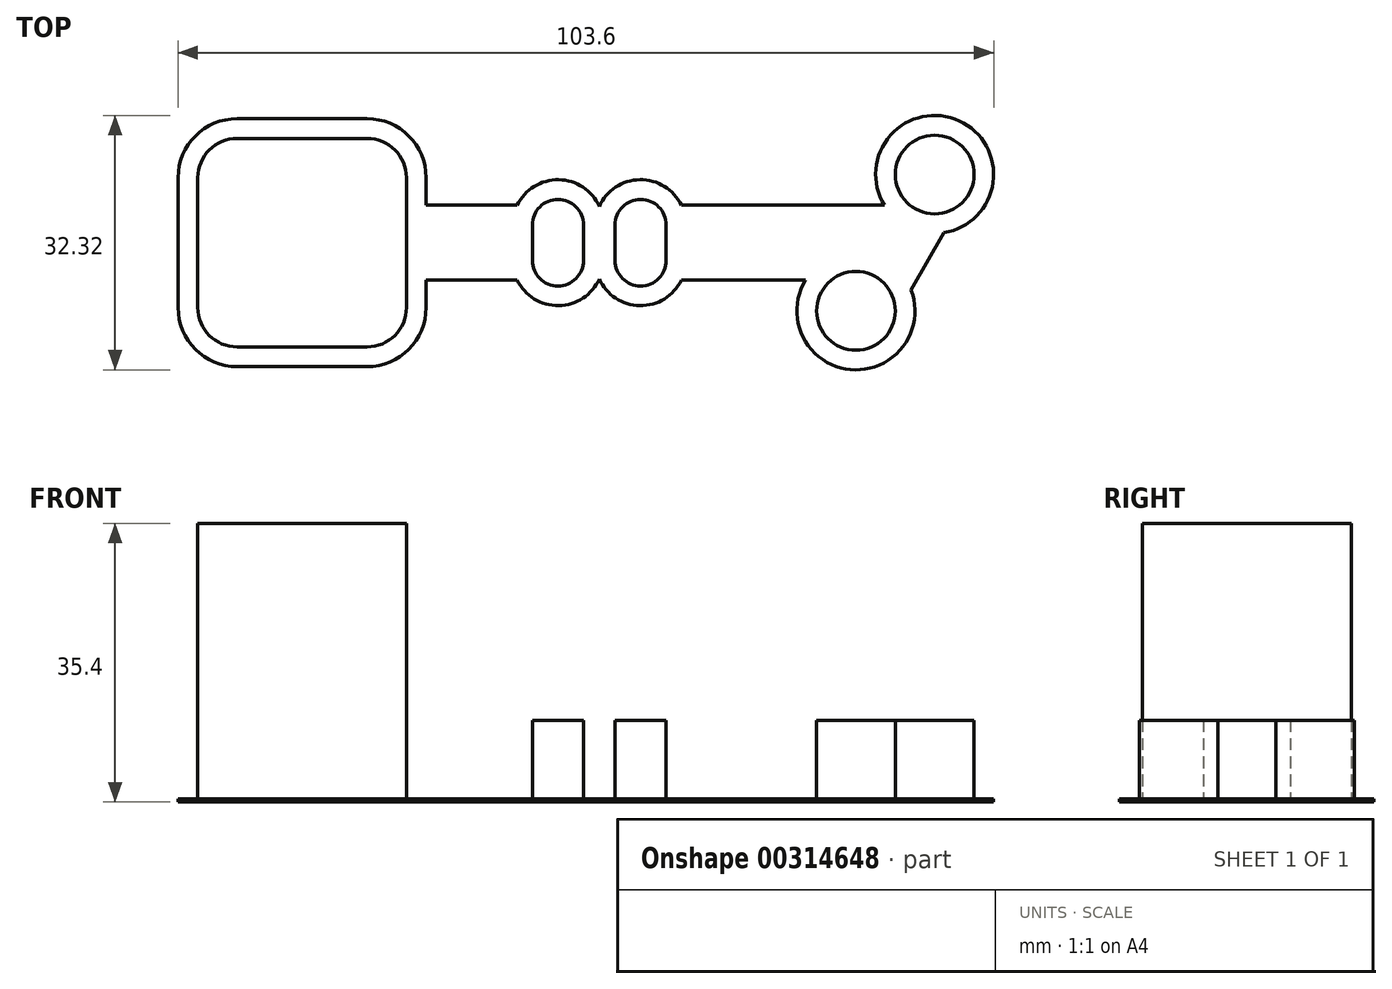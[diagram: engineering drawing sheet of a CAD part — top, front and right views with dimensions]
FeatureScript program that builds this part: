
annotation { "Feature Type Name" : "Feature", "Feature Type Description" : "" }
export const myFeature = defineFeature(function(context is Context, id is Id, definition is map)
    precondition{}
    {
        {
            var Q0;
            Q0=qCreatedBy(makeId("Top.planeOp"),FACE);
            var sketch = newSketch(context, id + "F0", { "sketchPlane" : qUnion([Q0])});
            skLineSegment(sketch, "E0.bottom", {"start": v(-8.25, 13.25) * mm, "end": v(8.25, 13.25) * mm});
            skLineSegment(sketch, "E0.top", {"start": v(-8.25, -13.25) * mm, "end": v(8.25, -13.25) * mm});
            skLineSegment(sketch, "E0.left", {"start": v(-13.25, 8.25) * mm, "end": v(-13.25, -8.25) * mm});
            skLineSegment(sketch, "E0.right", {"start": v(13.25, 8.25) * mm, "end": v(13.25, 2.25) * mm});
            skPoint(sketch, "E0.middle", {"position": v(0, 0) * mm});
            skPoint(sketch, "E1.visualSharp", {"position": v(-13.25, 13.25) * mm});
            skArc(sketch, "E1.filletArc", {"start": v(-8.25, 13.25) * mm, "mid": v(-11.79, 11.79) * mm, "end": v(-13.25, 8.25) * mm});
            skPoint(sketch, "E2.visualSharp", {"position": v(13.25, 13.25) * mm});
            skArc(sketch, "E2.filletArc", {"start": v(13.25, 8.25) * mm, "mid": v(11.79, 11.79) * mm, "end": v(8.25, 13.25) * mm});
            skPoint(sketch, "E3.visualSharp", {"position": v(13.25, -13.25) * mm});
            skArc(sketch, "E3.filletArc", {"start": v(8.25, -13.25) * mm, "mid": v(11.79, -11.79) * mm, "end": v(13.25, -8.25) * mm});
            skPoint(sketch, "E4.visualSharp", {"position": v(-13.25, -13.25) * mm});
            skArc(sketch, "E4.filletArc", {"start": v(-13.25, -8.25) * mm, "mid": v(-11.79, -11.79) * mm, "end": v(-8.25, -13.25) * mm});
            skCircle(sketch, "E5", {"center": v(0, 0) * mm, "radius": 4.5 * mm});
            skLineSegment(sketch, "E6", {"start": v(-4.5, 13.25) * mm, "end": v(-4.5, -13.25) * mm});
            skLineSegment(sketch, "E7", {"start": v(4.5, 13.25) * mm, "end": v(4.5, -13.25) * mm});
            skLineSegment(sketch, "E8", {"start": v(-13.25, 4.5) * mm, "end": v(13.25, 4.5) * mm});
            skLineSegment(sketch, "E9", {"start": v(-13.25, -4.5) * mm, "end": v(13.25, -4.5) * mm});
            skLineSegment(sketch, "E10", {"start": v(-40.84, 0) * mm, "end": v(98.04, 0) * mm, "construction": true});
            skPoint(sketch, "E10.startSnap0", {"position": v(-13.25, 0) * mm});
            skPoint(sketch, "E10.endSnap0", {"position": v(-13.25, 0) * mm});
            skLineSegment(sketch, "E11", {"start": v(13.25, 2.25) * mm, "end": v(29.25, 2.25) * mm});
            skLineSegment(sketch, "E12.bottom", {"start": v(29.25, 2.25) * mm, "end": v(35.75, 2.25) * mm});
            skLineSegment(sketch, "E12.top", {"start": v(29.25, -2.25) * mm, "end": v(35.75, -2.25) * mm});
            skLineSegment(sketch, "E12.left", {"start": v(29.25, 2.25) * mm, "end": v(29.25, -2.25) * mm});
            skLineSegment(sketch, "E12.right", {"start": v(35.75, 2.25) * mm, "end": v(35.75, -2.25) * mm});
            skLineSegment(sketch, "E13", {"start": v(37.75, 18.58) * mm, "end": v(37.75, -20.06) * mm, "construction": true});
            skLineSegment(sketch, "E14.MirrorCS", {"start": v(13.25, -2.25) * mm, "end": v(29.25, -2.25) * mm});
            skLineSegment(sketch, "E15.MirrorCS", {"start": v(46.25, 2.25) * mm, "end": v(39.75, 2.25) * mm});
            skLineSegment(sketch, "E16.MirrorCS", {"start": v(39.75, 2.25) * mm, "end": v(39.75, -2.25) * mm});
            skLineSegment(sketch, "E17.MirrorCS", {"start": v(46.25, -2.25) * mm, "end": v(39.75, -2.25) * mm});
            skLineSegment(sketch, "E18.MirrorCS", {"start": v(46.25, 2.25) * mm, "end": v(46.25, -2.25) * mm});
            skArc(sketch, "E19", {"start": v(29.25, 2.25) * mm, "mid": v(32.5, 5.5) * mm, "end": v(35.75, 2.25) * mm});
            skArc(sketch, "E20.MirrorCS", {"start": v(29.25, -2.25) * mm, "mid": v(32.5, -5.5) * mm, "end": v(35.75, -2.25) * mm});
            skArc(sketch, "E21.MirrorCS", {"start": v(46.25, 2.25) * mm, "mid": v(43, 5.5) * mm, "end": v(39.75, 2.25) * mm});
            skArc(sketch, "E22.MirrorCS", {"start": v(46.25, -2.25) * mm, "mid": v(43, -5.5) * mm, "end": v(39.75, -2.25) * mm});
            skLineSegment(sketch, "E23", {"start": v(35.75, 2.25) * mm, "end": v(39.75, 2.25) * mm});
            skLineSegment(sketch, "E24", {"start": v(39.75, -2.25) * mm, "end": v(35.75, -2.25) * mm});
            skLineSegment(sketch, "E25", {"start": v(46.25, 2.25) * mm, "end": v(74.05, 2.25) * mm});
            skLineSegment(sketch, "E26", {"start": v(80.35, 8.66) * mm, "end": v(70.35, -8.66) * mm, "construction": true});
            skPoint(sketch, "E27", {"position": v(75.35, 0) * mm});
            skLineSegment(sketch, "E28", {"start": v(76.17, 5.92) * mm, "end": v(74.05, 2.25) * mm});
            skLineSegment(sketch, "E29.MirrorCS", {"start": v(80.06, 3.67) * mm, "end": v(74.53, -5.92) * mm});
            skLineSegment(sketch, "E30.MirrorCS", {"start": v(46.25, -2.25) * mm, "end": v(71.45, -2.25) * mm});
            skPoint(sketch, "E31.orphan", {"position": v(72.75, -2.25) * mm});
            skPoint(sketch, "E32", {"position": v(72.75, 0) * mm});
            skLineSegment(sketch, "E33", {"start": v(13.25, 2.25) * mm, "end": v(13.25, -2.25) * mm});
            skLineSegment(sketch, "E34", {"start": v(13.25, -2.25) * mm, "end": v(13.25, -8.25) * mm});
            skArc(sketch, "E35", {"start": v(76.17, 5.92) * mm, "mid": v(77.85, 4.33) * mm, "end": v(80.06, 3.67) * mm});
            skArc(sketch, "E36", {"start": v(80.06, 3.67) * mm, "mid": v(82.85, 13) * mm, "end": v(76.17, 5.92) * mm});
            skArc(sketch, "E37", {"start": v(70.63, -3.67) * mm, "mid": v(67.85, -13) * mm, "end": v(74.53, -5.92) * mm});
            skArc(sketch, "E38", {"start": v(74.53, -5.92) * mm, "mid": v(72.85, -4.33) * mm, "end": v(70.63, -3.67) * mm});
            skLineSegment(sketch, "E39", {"start": v(74.05, 2.25) * mm, "end": v(71.45, -2.25) * mm});
            skLineSegment(sketch, "E40", {"start": v(71.45, -2.25) * mm, "end": v(70.63, -3.67) * mm});
            skLineSegment(sketch, "E41.0", {"start": v(15.75, 8.25) * mm, "end": v(15.75, 4.75) * mm});
            skLineSegment(sketch, "E41.1", {"start": v(15.75, 4.75) * mm, "end": v(27.32, 4.75) * mm});
            skArc(sketch, "E41.2", {"start": v(27.32, 4.75) * mm, "mid": v(32.59, 8) * mm, "end": v(37.75, 4.6) * mm});
            skArc(sketch, "E41.3", {"start": v(48.18, 4.75) * mm, "mid": v(42.91, 8) * mm, "end": v(37.75, 4.6) * mm});
            skLineSegment(sketch, "E41.4", {"start": v(48.18, 4.75) * mm, "end": v(73.95, 4.75) * mm});
            skArc(sketch, "E41.5", {"start": v(15.75, 8.25) * mm, "mid": v(13.55, 13.55) * mm, "end": v(8.25, 15.75) * mm});
            skArc(sketch, "E41.6", {"start": v(81.56, 1.26) * mm, "mid": v(83.47, 15.48) * mm, "end": v(73.95, 4.75) * mm});
            skLineSegment(sketch, "E41.7", {"start": v(81.56, 1.26) * mm, "end": v(77.36, -6) * mm});
            skArc(sketch, "E41.8", {"start": v(63.95, -4.75) * mm, "mid": v(69.65, -16.13) * mm, "end": v(77.36, -6) * mm});
            skLineSegment(sketch, "E41.9", {"start": v(48.18, -4.75) * mm, "end": v(63.95, -4.75) * mm});
            skArc(sketch, "E41.10", {"start": v(-15.75, -8.25) * mm, "mid": v(-13.55, -13.55) * mm, "end": v(-8.25, -15.75) * mm});
            skLineSegment(sketch, "E41.11", {"start": v(-15.75, 8.25) * mm, "end": v(-15.75, -8.25) * mm});
            skArc(sketch, "E41.12", {"start": v(-8.25, 15.75) * mm, "mid": v(-13.55, 13.55) * mm, "end": v(-15.75, 8.25) * mm});
            skLineSegment(sketch, "E41.13", {"start": v(-8.25, 15.75) * mm, "end": v(8.25, 15.75) * mm});
            skLineSegment(sketch, "E41.14", {"start": v(-8.25, -15.75) * mm, "end": v(8.25, -15.75) * mm});
            skArc(sketch, "E41.15", {"start": v(8.25, -15.75) * mm, "mid": v(13.55, -13.55) * mm, "end": v(15.75, -8.25) * mm});
            skLineSegment(sketch, "E41.16", {"start": v(15.75, -4.75) * mm, "end": v(15.75, -8.25) * mm});
            skLineSegment(sketch, "E41.17", {"start": v(15.75, -4.75) * mm, "end": v(27.32, -4.75) * mm});
            skArc(sketch, "E41.18", {"start": v(27.32, -4.75) * mm, "mid": v(32.59, -8) * mm, "end": v(37.75, -4.6) * mm});
            skArc(sketch, "E41.19", {"start": v(48.18, -4.75) * mm, "mid": v(42.91, -8) * mm, "end": v(37.75, -4.6) * mm});
            skSolve(sketch);
        }
        {
            var Q0;
            {var subQ5=sQuery(id+"F0.wireOp",EDGE,"E4.filletArc");Q0=makeQuery(id+"F0.imprint","IMPRINT",FACE,{"disambiguationData":[TD([[makeQuery(id+"F0.imprint","IMPRINT",EDGE,{"derivedFrom":subQ5}),1.0]])]});}
            var Q1;
            {var subQ5=sQuery(id+"F0.wireOp",EDGE,"E2.filletArc");Q1=makeQuery(id+"F0.imprint","IMPRINT",FACE,{"disambiguationData":[TD([[makeQuery(id+"F0.imprint","IMPRINT",EDGE,{"derivedFrom":subQ5}),1.0]])]});}
            var Q2;
            {var subQ0=sQuery(id+"F0.wireOp",EDGE,"E8");var subQ1=sQuery(id+"F0.wireOp",EDGE,"E5");var subQ2=makeQuery(id+"F0.imprint","INTERSECT",VERTEX,{"derivedFrom":[subQ1,subQ0]});Q2=makeQuery(id+"F0.imprint","IMPRINT",FACE,{"disambiguationData":[TD([[makeQuery(id+"F0.imprint","IMPRINT",EDGE,{"disambiguationData":[TD([[subQ2,1.0]])],"derivedFrom":subQ1}),-1.0]])]});}
            var Q3;
            {var subQ7=sQuery(id+"F0.wireOp",EDGE,"E3.filletArc");Q3=makeQuery(id+"F0.imprint","IMPRINT",FACE,{"disambiguationData":[TD([[makeQuery(id+"F0.imprint","IMPRINT",EDGE,{"derivedFrom":subQ7}),1.0]])]});}
            var Q4;
            {var subQ0=sQuery(id+"F0.wireOp",EDGE,"E8");var subQ1=sQuery(id+"F0.wireOp",EDGE,"E5");var subQ2=makeQuery(id+"F0.imprint","INTERSECT",VERTEX,{"derivedFrom":[subQ1,subQ0]});Q4=makeQuery(id+"F0.imprint","IMPRINT",FACE,{"disambiguationData":[TD([[makeQuery(id+"F0.imprint","IMPRINT",EDGE,{"disambiguationData":[TD([[subQ2,-1.0]])],"derivedFrom":subQ1}),-1.0]])]});}
            var Q5;
            Q5=makeQuery(id+"F0.imprint","IMPRINT",FACE,{"disambiguationData":[TD([[makeQuery(id+"F0.imprint","IMPRINT",EDGE,{"derivedFrom":sQuery(id+"F0.wireOp",EDGE,"E28")}),1.0]])]});
            var Q6;
            Q6=makeQuery(id+"F0.imprint","IMPRINT",FACE,{"disambiguationData":[TD([[makeQuery(id+"F0.imprint","IMPRINT",EDGE,{"derivedFrom":sQuery(id+"F0.wireOp",EDGE,"E35")}),1.0]])]});
            var Q7;
            Q7=makeQuery(id+"F0.imprint","IMPRINT",FACE,{"disambiguationData":[TD([[makeQuery(id+"F0.imprint","IMPRINT",EDGE,{"derivedFrom":sQuery(id+"F0.wireOp",EDGE,"E17.MirrorCS")}),1.0]])]});
            var Q8;
            {var subQ5=sQuery(id+"F0.wireOp",EDGE,"E1.filletArc");Q8=makeQuery(id+"F0.imprint","IMPRINT",FACE,{"disambiguationData":[TD([[makeQuery(id+"F0.imprint","IMPRINT",EDGE,{"derivedFrom":subQ5}),1.0]])]});}
            var Q9;
            {var subQ0=sQuery(id+"F0.wireOp",EDGE,"E6");var subQ1=sQuery(id+"F0.wireOp",EDGE,"E5");var subQ2=makeQuery(id+"F0.imprint","INTERSECT",VERTEX,{"derivedFrom":[subQ1,subQ0]});Q9=makeQuery(id+"F0.imprint","IMPRINT",FACE,{"disambiguationData":[TD([[makeQuery(id+"F0.imprint","IMPRINT",EDGE,{"disambiguationData":[TD([[subQ2,-1.0]])],"derivedFrom":subQ1}),-1.0]])]});}
            var Q10;
            Q10=makeQuery(id+"F0.imprint","IMPRINT",FACE,{"disambiguationData":[TD([[makeQuery(id+"F0.imprint","IMPRINT",EDGE,{"derivedFrom":sQuery(id+"F0.wireOp",EDGE,"E12.bottom")}),1.0]])]});
            var Q11;
            Q11=makeQuery(id+"F0.imprint","IMPRINT",FACE,{"disambiguationData":[TD([[makeQuery(id+"F0.imprint","IMPRINT",EDGE,{"derivedFrom":sQuery(id+"F0.wireOp",EDGE,"E12.top")}),-1.0]])]});
            var Q12;
            {var subQ1=sQuery(id+"F0.wireOp",EDGE,"E0.top");var subQ5=sQuery(id+"F0.wireOp",EDGE,"E6");var subQ6=makeQuery(id+"F0.imprint","INTERSECT",VERTEX,{"derivedFrom":[subQ1,subQ5]});Q12=makeQuery(id+"F0.imprint","IMPRINT",FACE,{"disambiguationData":[TD([[makeQuery(id+"F0.imprint","IMPRINT",EDGE,{"disambiguationData":[TD([[subQ6,-1.0]])],"derivedFrom":subQ1}),1.0]])]});}
            var Q13;
            Q13=makeQuery(id+"F0.imprint","IMPRINT",FACE,{"disambiguationData":[TD([[makeQuery(id+"F0.imprint","IMPRINT",EDGE,{"derivedFrom":sQuery(id+"F0.wireOp",EDGE,"E12.right")}),1.0]])]});
            var Q14;
            {var subQ4=sQuery(id+"F0.wireOp",EDGE,"E8");var subQ6=sQuery(id+"F0.wireOp",EDGE,"E0.left");var subQ8=makeQuery(id+"F0.imprint","INTERSECT",VERTEX,{"derivedFrom":[subQ6,subQ4]});Q14=makeQuery(id+"F0.imprint","IMPRINT",FACE,{"disambiguationData":[TD([[makeQuery(id+"F0.imprint","IMPRINT",EDGE,{"disambiguationData":[TD([[subQ8,-1.0]])],"derivedFrom":subQ6}),1.0]])]});}
            var Q15;
            Q15=makeQuery(id+"F0.imprint","IMPRINT",FACE,{"disambiguationData":[TD([[makeQuery(id+"F0.imprint","IMPRINT",EDGE,{"derivedFrom":sQuery(id+"F0.wireOp",EDGE,"E18.MirrorCS")}),1.0]])]});
            var Q16;
            Q16=makeQuery(id+"F0.imprint","IMPRINT",FACE,{"disambiguationData":[TD([[makeQuery(id+"F0.imprint","IMPRINT",EDGE,{"derivedFrom":sQuery(id+"F0.wireOp",EDGE,"E37")}),1.0]])]});
            var Q17;
            Q17=makeQuery(id+"F0.imprint","IMPRINT",FACE,{"disambiguationData":[TD([[makeQuery(id+"F0.imprint","IMPRINT",EDGE,{"derivedFrom":sQuery(id+"F0.wireOp",EDGE,"E11")}),-1.0]])]});
            var Q18;
            {var subQ0=sQuery(id+"F0.wireOp",EDGE,"E5");var subQ1=makeQuery(id+"F0.imprint","INTERSECT",VERTEX,{"derivedFrom":[subQ0,sQuery(id+"F0.wireOp",EDGE,"E8")]});Q18=makeQuery(id+"F0.imprint","IMPRINT",FACE,{"disambiguationData":[TD([[makeQuery(id+"F0.imprint","IMPRINT",EDGE,{"disambiguationData":[TD([[subQ1,1.0]])],"derivedFrom":subQ0}),1.0]])]});}
            var Q19;
            Q19=makeQuery(id+"F0.imprint","IMPRINT",FACE,{"disambiguationData":[TD([[makeQuery(id+"F0.imprint","IMPRINT",EDGE,{"derivedFrom":sQuery(id+"F0.wireOp",EDGE,"E15.MirrorCS")}),-1.0]])]});
            var Q20;
            {var subQ0=sQuery(id+"F0.wireOp",EDGE,"E7");var subQ1=sQuery(id+"F0.wireOp",EDGE,"E5");var subQ2=makeQuery(id+"F0.imprint","INTERSECT",VERTEX,{"derivedFrom":[subQ1,subQ0]});Q20=makeQuery(id+"F0.imprint","IMPRINT",FACE,{"disambiguationData":[TD([[makeQuery(id+"F0.imprint","IMPRINT",EDGE,{"disambiguationData":[TD([[subQ2,1.0]])],"derivedFrom":subQ1}),-1.0]])]});}
            var Q21;
            {var subQ2=sQuery(id+"F0.wireOp",EDGE,"E6");var subQ5=sQuery(id+"F0.wireOp",EDGE,"E0.bottom");var subQ8=makeQuery(id+"F0.imprint","INTERSECT",VERTEX,{"derivedFrom":[subQ5,subQ2]});Q21=makeQuery(id+"F0.imprint","IMPRINT",FACE,{"disambiguationData":[TD([[makeQuery(id+"F0.imprint","IMPRINT",EDGE,{"disambiguationData":[TD([[subQ8,-1.0]])],"derivedFrom":subQ5}),-1.0]])]});}
            var Q22;
            Q22=makeQuery(id+"F0.imprint","IMPRINT",FACE,{"disambiguationData":[TD([[makeQuery(id+"F0.imprint","IMPRINT",EDGE,{"derivedFrom":sQuery(id+"F0.wireOp",EDGE,"E15.MirrorCS")}),1.0]])]});
            var Q23;
            {var subQ8=sQuery(id+"F0.wireOp",EDGE,"E33");Q23=makeQuery(id+"F0.imprint","IMPRINT",FACE,{"disambiguationData":[TD([[makeQuery(id+"F0.imprint","IMPRINT",EDGE,{"derivedFrom":subQ8}),-1.0]])]});}
            var Q24;
            Q24=makeQuery(id+"F0.imprint","IMPRINT",FACE,{"disambiguationData":[TD([[makeQuery(id+"F0.imprint","IMPRINT",EDGE,{"derivedFrom":sQuery(id+"F0.wireOp",EDGE,"E12.bottom")}),-1.0]])]});
            var Q25;
            {var subQ13=sQuery(id+"F0.wireOp",EDGE,"E1.filletArc");Q25=makeQuery(id+"F0.imprint","IMPRINT",FACE,{"disambiguationData":[TD([[makeQuery(id+"F0.imprint","IMPRINT",EDGE,{"derivedFrom":subQ13}),-1.0]])]});}
            extrude(context, id + "F1", {"entities" : qUnion([Q0, Q1, Q2, Q3, Q4, Q5, Q6, Q7, Q8, Q9, Q10, Q11, Q12, Q13, Q14, Q15, Q16, Q17, Q18, Q19, Q20, Q21, Q22, Q23, Q24, Q25]), "depth" : 0.4 * mm});
        }
        {
            var Q0;
            Q0=makeQuery(id+"F1.opExtrude","CAP_FACE",FACE,{"disambiguationData":[OSD([sQuery(id+"F0.wireOp",EDGE,"E41.0"),sQuery(id+"F0.wireOp",EDGE,"E41.1"),sQuery(id+"F0.wireOp",EDGE,"E41.2"),sQuery(id+"F0.wireOp",EDGE,"E41.3"),sQuery(id+"F0.wireOp",EDGE,"E41.4"),sQuery(id+"F0.wireOp",EDGE,"E41.5"),sQuery(id+"F0.wireOp",EDGE,"E41.6"),sQuery(id+"F0.wireOp",EDGE,"E41.7"),sQuery(id+"F0.wireOp",EDGE,"E41.8"),sQuery(id+"F0.wireOp",EDGE,"E41.9"),sQuery(id+"F0.wireOp",EDGE,"E41.10"),sQuery(id+"F0.wireOp",EDGE,"E41.11"),sQuery(id+"F0.wireOp",EDGE,"E41.12"),sQuery(id+"F0.wireOp",EDGE,"E41.13"),sQuery(id+"F0.wireOp",EDGE,"E41.14"),sQuery(id+"F0.wireOp",EDGE,"E41.15"),sQuery(id+"F0.wireOp",EDGE,"E41.16"),sQuery(id+"F0.wireOp",EDGE,"E41.17"),sQuery(id+"F0.wireOp",EDGE,"E41.18"),sQuery(id+"F0.wireOp",EDGE,"E41.19")])],"isStart":false});
            var sketch = newSketch(context, id + "F2", { "sketchPlane" : qUnion([Q0])});
            skLineSegment(sketch, "E42.0", {"start": v(-8.25, 13.25) * mm, "end": v(8.25, 13.25) * mm});
            skLineSegment(sketch, "E42.1", {"start": v(-8.25, -13.25) * mm, "end": v(8.25, -13.25) * mm});
            skLineSegment(sketch, "E42.2", {"start": v(-13.25, 8.25) * mm, "end": v(-13.25, -8.25) * mm});
            skLineSegment(sketch, "E42.3", {"start": v(13.25, 8.25) * mm, "end": v(13.25, 2.25) * mm});
            skPoint(sketch, "E42.4", {"position": v(0, 0) * mm});
            skPoint(sketch, "E42.5", {"position": v(-13.25, 13.25) * mm});
            skArc(sketch, "E42.6", {"start": v(-8.25, 13.25) * mm, "mid": v(-11.79, 11.79) * mm, "end": v(-13.25, 8.25) * mm});
            skPoint(sketch, "E42.7", {"position": v(13.25, 13.25) * mm});
            skArc(sketch, "E42.8", {"start": v(13.25, 8.25) * mm, "mid": v(11.79, 11.79) * mm, "end": v(8.25, 13.25) * mm});
            skPoint(sketch, "E42.9", {"position": v(13.25, -13.25) * mm});
            skArc(sketch, "E42.10", {"start": v(8.25, -13.25) * mm, "mid": v(11.79, -11.79) * mm, "end": v(13.25, -8.25) * mm});
            skPoint(sketch, "E42.11", {"position": v(-13.25, -13.25) * mm});
            skArc(sketch, "E42.12", {"start": v(-13.25, -8.25) * mm, "mid": v(-11.79, -11.79) * mm, "end": v(-8.25, -13.25) * mm});
            skCircle(sketch, "E42.13", {"center": v(0, 0) * mm, "radius": 4.5 * mm});
            skLineSegment(sketch, "E42.14", {"start": v(-4.5, 13.25) * mm, "end": v(-4.5, -13.25) * mm});
            skLineSegment(sketch, "E42.15", {"start": v(4.5, 13.25) * mm, "end": v(4.5, -13.25) * mm});
            skLineSegment(sketch, "E42.16", {"start": v(-13.25, 4.5) * mm, "end": v(13.25, 4.5) * mm});
            skLineSegment(sketch, "E42.17", {"start": v(-13.25, -4.5) * mm, "end": v(13.25, -4.5) * mm});
            skPoint(sketch, "E42.19", {"position": v(-13.25, 0) * mm});
            skPoint(sketch, "E42.20", {"position": v(-13.25, 0) * mm});
            skLineSegment(sketch, "E42.21", {"start": v(13.25, 2.25) * mm, "end": v(29.25, 2.25) * mm});
            skLineSegment(sketch, "E42.22", {"start": v(29.25, 2.25) * mm, "end": v(35.75, 2.25) * mm});
            skLineSegment(sketch, "E42.23", {"start": v(29.25, -2.25) * mm, "end": v(35.75, -2.25) * mm});
            skLineSegment(sketch, "E42.24", {"start": v(29.25, 2.25) * mm, "end": v(29.25, -2.25) * mm});
            skLineSegment(sketch, "E42.25", {"start": v(35.75, 2.25) * mm, "end": v(35.75, -2.25) * mm});
            skLineSegment(sketch, "E42.27", {"start": v(13.25, -2.25) * mm, "end": v(29.25, -2.25) * mm});
            skLineSegment(sketch, "E42.28", {"start": v(46.25, 2.25) * mm, "end": v(39.75, 2.25) * mm});
            skLineSegment(sketch, "E42.29", {"start": v(39.75, 2.25) * mm, "end": v(39.75, -2.25) * mm});
            skLineSegment(sketch, "E42.30", {"start": v(46.25, -2.25) * mm, "end": v(39.75, -2.25) * mm});
            skLineSegment(sketch, "E42.31", {"start": v(46.25, 2.25) * mm, "end": v(46.25, -2.25) * mm});
            skArc(sketch, "E42.32", {"start": v(29.25, 2.25) * mm, "mid": v(32.5, 5.5) * mm, "end": v(35.75, 2.25) * mm});
            skArc(sketch, "E42.33", {"start": v(29.25, -2.25) * mm, "mid": v(32.5, -5.5) * mm, "end": v(35.75, -2.25) * mm});
            skArc(sketch, "E42.34", {"start": v(46.25, 2.25) * mm, "mid": v(43, 5.5) * mm, "end": v(39.75, 2.25) * mm});
            skArc(sketch, "E42.35", {"start": v(46.25, -2.25) * mm, "mid": v(43, -5.5) * mm, "end": v(39.75, -2.25) * mm});
            skLineSegment(sketch, "E42.36", {"start": v(35.75, 2.25) * mm, "end": v(39.75, 2.25) * mm});
            skLineSegment(sketch, "E42.37", {"start": v(39.75, -2.25) * mm, "end": v(35.75, -2.25) * mm});
            skLineSegment(sketch, "E42.38", {"start": v(46.25, 2.25) * mm, "end": v(74.05, 2.25) * mm});
            skLineSegment(sketch, "E42.39", {"start": v(80.35, 8.66) * mm, "end": v(70.35, -8.66) * mm});
            skPoint(sketch, "E42.40", {"position": v(75.35, 0) * mm});
            skLineSegment(sketch, "E42.41", {"start": v(76.17, 5.92) * mm, "end": v(74.05, 2.25) * mm});
            skLineSegment(sketch, "E42.42", {"start": v(80.06, 3.67) * mm, "end": v(74.53, -5.92) * mm});
            skLineSegment(sketch, "E42.43", {"start": v(46.25, -2.25) * mm, "end": v(71.45, -2.25) * mm});
            skPoint(sketch, "E42.44", {"position": v(72.75, -2.25) * mm});
            skPoint(sketch, "E42.45", {"position": v(72.75, 0) * mm});
            skLineSegment(sketch, "E42.46", {"start": v(13.25, 2.25) * mm, "end": v(13.25, -2.25) * mm});
            skLineSegment(sketch, "E42.47", {"start": v(13.25, -2.25) * mm, "end": v(13.25, -8.25) * mm});
            skArc(sketch, "E42.48", {"start": v(76.17, 5.92) * mm, "mid": v(77.85, 4.33) * mm, "end": v(80.06, 3.67) * mm});
            skArc(sketch, "E42.49", {"start": v(80.06, 3.67) * mm, "mid": v(82.85, 13) * mm, "end": v(76.17, 5.92) * mm});
            skArc(sketch, "E42.50", {"start": v(70.63, -3.67) * mm, "mid": v(67.85, -13) * mm, "end": v(74.53, -5.92) * mm});
            skArc(sketch, "E42.51", {"start": v(74.53, -5.92) * mm, "mid": v(72.85, -4.33) * mm, "end": v(70.63, -3.67) * mm});
            skLineSegment(sketch, "E42.52", {"start": v(74.05, 2.25) * mm, "end": v(71.45, -2.25) * mm});
            skLineSegment(sketch, "E42.53", {"start": v(71.45, -2.25) * mm, "end": v(70.63, -3.67) * mm});
            skLineSegment(sketch, "E42.54", {"start": v(15.75, 8.25) * mm, "end": v(15.75, 4.75) * mm});
            skLineSegment(sketch, "E42.55", {"start": v(15.75, 4.75) * mm, "end": v(27.32, 4.75) * mm});
            skArc(sketch, "E42.56", {"start": v(27.32, 4.75) * mm, "mid": v(32.59, 8) * mm, "end": v(37.75, 4.6) * mm});
            skArc(sketch, "E42.57", {"start": v(48.18, 4.75) * mm, "mid": v(42.91, 8) * mm, "end": v(37.75, 4.6) * mm});
            skLineSegment(sketch, "E42.58", {"start": v(48.18, 4.75) * mm, "end": v(73.95, 4.75) * mm});
            skArc(sketch, "E42.59", {"start": v(15.75, 8.25) * mm, "mid": v(13.55, 13.55) * mm, "end": v(8.25, 15.75) * mm});
            skArc(sketch, "E42.60", {"start": v(81.56, 1.26) * mm, "mid": v(83.47, 15.48) * mm, "end": v(73.95, 4.75) * mm});
            skLineSegment(sketch, "E42.61", {"start": v(81.56, 1.26) * mm, "end": v(77.36, -6) * mm});
            skArc(sketch, "E42.62", {"start": v(63.95, -4.75) * mm, "mid": v(69.65, -16.13) * mm, "end": v(77.36, -6) * mm});
            skLineSegment(sketch, "E42.63", {"start": v(48.18, -4.75) * mm, "end": v(63.95, -4.75) * mm});
            skArc(sketch, "E42.64", {"start": v(-15.75, -8.25) * mm, "mid": v(-13.55, -13.55) * mm, "end": v(-8.25, -15.75) * mm});
            skLineSegment(sketch, "E42.65", {"start": v(-15.75, 8.25) * mm, "end": v(-15.75, -8.25) * mm});
            skArc(sketch, "E42.66", {"start": v(-8.25, 15.75) * mm, "mid": v(-13.55, 13.55) * mm, "end": v(-15.75, 8.25) * mm});
            skLineSegment(sketch, "E42.67", {"start": v(-8.25, 15.75) * mm, "end": v(8.25, 15.75) * mm});
            skLineSegment(sketch, "E42.68", {"start": v(-8.25, -15.75) * mm, "end": v(8.25, -15.75) * mm});
            skArc(sketch, "E42.69", {"start": v(8.25, -15.75) * mm, "mid": v(13.55, -13.55) * mm, "end": v(15.75, -8.25) * mm});
            skLineSegment(sketch, "E42.70", {"start": v(15.75, -4.75) * mm, "end": v(15.75, -8.25) * mm});
            skLineSegment(sketch, "E42.71", {"start": v(15.75, -4.75) * mm, "end": v(27.32, -4.75) * mm});
            skArc(sketch, "E42.72", {"start": v(27.32, -4.75) * mm, "mid": v(32.59, -8) * mm, "end": v(37.75, -4.6) * mm});
            skArc(sketch, "E42.73", {"start": v(48.18, -4.75) * mm, "mid": v(42.91, -8) * mm, "end": v(37.75, -4.6) * mm});
            skSolve(sketch);
        }
        {
            var Q0;
            {var subQ5=sQuery(id+"F2.wireOp",EDGE,"E42.6");Q0=makeQuery(id+"F2.imprint","IMPRINT",FACE,{"disambiguationData":[TD([[makeQuery(id+"F2.imprint","IMPRINT",EDGE,{"derivedFrom":subQ5}),1.0]])]});}
            var Q1;
            {var subQ2=sQuery(id+"F2.wireOp",EDGE,"E42.14");var subQ5=sQuery(id+"F2.wireOp",EDGE,"E42.0");var subQ8=makeQuery(id+"F2.imprint","INTERSECT",VERTEX,{"derivedFrom":[subQ5,subQ2]});Q1=makeQuery(id+"F2.imprint","IMPRINT",FACE,{"disambiguationData":[TD([[makeQuery(id+"F2.imprint","IMPRINT",EDGE,{"disambiguationData":[TD([[subQ8,-1.0]])],"derivedFrom":subQ5}),-1.0]])]});}
            var Q2;
            {var subQ5=sQuery(id+"F2.wireOp",EDGE,"E42.8");Q2=makeQuery(id+"F2.imprint","IMPRINT",FACE,{"disambiguationData":[TD([[makeQuery(id+"F2.imprint","IMPRINT",EDGE,{"derivedFrom":subQ5}),1.0]])]});}
            var Q3;
            {var subQ7=sQuery(id+"F2.wireOp",EDGE,"E42.46");Q3=makeQuery(id+"F2.imprint","IMPRINT",FACE,{"disambiguationData":[TD([[makeQuery(id+"F2.imprint","IMPRINT",EDGE,{"derivedFrom":subQ7}),-1.0]])]});}
            var Q4;
            {var subQ7=sQuery(id+"F2.wireOp",EDGE,"E42.10");Q4=makeQuery(id+"F2.imprint","IMPRINT",FACE,{"disambiguationData":[TD([[makeQuery(id+"F2.imprint","IMPRINT",EDGE,{"derivedFrom":subQ7}),1.0]])]});}
            var Q5;
            {var subQ1=sQuery(id+"F2.wireOp",EDGE,"E42.1");var subQ5=sQuery(id+"F2.wireOp",EDGE,"E42.14");var subQ6=makeQuery(id+"F2.imprint","INTERSECT",VERTEX,{"derivedFrom":[subQ1,subQ5]});Q5=makeQuery(id+"F2.imprint","IMPRINT",FACE,{"disambiguationData":[TD([[makeQuery(id+"F2.imprint","IMPRINT",EDGE,{"disambiguationData":[TD([[subQ6,-1.0]])],"derivedFrom":subQ1}),1.0]])]});}
            var Q6;
            {var subQ5=sQuery(id+"F2.wireOp",EDGE,"E42.12");Q6=makeQuery(id+"F2.imprint","IMPRINT",FACE,{"disambiguationData":[TD([[makeQuery(id+"F2.imprint","IMPRINT",EDGE,{"derivedFrom":subQ5}),1.0]])]});}
            var Q7;
            {var subQ4=sQuery(id+"F2.wireOp",EDGE,"E42.16");var subQ6=sQuery(id+"F2.wireOp",EDGE,"E42.2");var subQ8=makeQuery(id+"F2.imprint","INTERSECT",VERTEX,{"derivedFrom":[subQ6,subQ4]});Q7=makeQuery(id+"F2.imprint","IMPRINT",FACE,{"disambiguationData":[TD([[makeQuery(id+"F2.imprint","IMPRINT",EDGE,{"disambiguationData":[TD([[subQ8,-1.0]])],"derivedFrom":subQ6}),1.0]])]});}
            var Q8;
            {var subQ0=sQuery(id+"F2.wireOp",EDGE,"E42.16");var subQ1=sQuery(id+"F2.wireOp",EDGE,"E42.13");var subQ2=makeQuery(id+"F2.imprint","INTERSECT",VERTEX,{"derivedFrom":[subQ1,subQ0]});Q8=makeQuery(id+"F2.imprint","IMPRINT",FACE,{"disambiguationData":[TD([[makeQuery(id+"F2.imprint","IMPRINT",EDGE,{"disambiguationData":[TD([[subQ2,1.0]])],"derivedFrom":subQ1}),-1.0]])]});}
            var Q9;
            {var subQ0=sQuery(id+"F2.wireOp",EDGE,"E42.15");var subQ1=sQuery(id+"F2.wireOp",EDGE,"E42.13");var subQ2=makeQuery(id+"F2.imprint","INTERSECT",VERTEX,{"derivedFrom":[subQ1,subQ0]});Q9=makeQuery(id+"F2.imprint","IMPRINT",FACE,{"disambiguationData":[TD([[makeQuery(id+"F2.imprint","IMPRINT",EDGE,{"disambiguationData":[TD([[subQ2,1.0]])],"derivedFrom":subQ1}),-1.0]])]});}
            var Q10;
            {var subQ0=sQuery(id+"F2.wireOp",EDGE,"E42.14");var subQ1=sQuery(id+"F2.wireOp",EDGE,"E42.13");var subQ2=makeQuery(id+"F2.imprint","INTERSECT",VERTEX,{"derivedFrom":[subQ1,subQ0]});Q10=makeQuery(id+"F2.imprint","IMPRINT",FACE,{"disambiguationData":[TD([[makeQuery(id+"F2.imprint","IMPRINT",EDGE,{"disambiguationData":[TD([[subQ2,-1.0]])],"derivedFrom":subQ1}),-1.0]])]});}
            var Q11;
            {var subQ0=sQuery(id+"F2.wireOp",EDGE,"E42.16");var subQ1=sQuery(id+"F2.wireOp",EDGE,"E42.13");var subQ2=makeQuery(id+"F2.imprint","INTERSECT",VERTEX,{"derivedFrom":[subQ1,subQ0]});Q11=makeQuery(id+"F2.imprint","IMPRINT",FACE,{"disambiguationData":[TD([[makeQuery(id+"F2.imprint","IMPRINT",EDGE,{"disambiguationData":[TD([[subQ2,-1.0]])],"derivedFrom":subQ1}),-1.0]])]});}
            var Q12;
            {var subQ0=sQuery(id+"F2.wireOp",EDGE,"E42.13");var subQ1=makeQuery(id+"F2.imprint","INTERSECT",VERTEX,{"derivedFrom":[subQ0,sQuery(id+"F2.wireOp",EDGE,"E42.16")]});Q12=makeQuery(id+"F2.imprint","IMPRINT",FACE,{"disambiguationData":[TD([[makeQuery(id+"F2.imprint","IMPRINT",EDGE,{"disambiguationData":[TD([[subQ1,1.0]])],"derivedFrom":subQ0}),1.0]])]});}
            var Q13;
            Q13=makeQuery(id+"F2.imprint","IMPRINT",FACE,{"disambiguationData":[TD([[makeQuery(id+"F2.imprint","IMPRINT",EDGE,{"derivedFrom":sQuery(id+"F2.wireOp",EDGE,"E42.22")}),-1.0]])]});
            var Q14;
            Q14=makeQuery(id+"F2.imprint","IMPRINT",FACE,{"disambiguationData":[TD([[makeQuery(id+"F2.imprint","IMPRINT",EDGE,{"derivedFrom":sQuery(id+"F2.wireOp",EDGE,"E42.22")}),1.0]])]});
            var Q15;
            Q15=makeQuery(id+"F2.imprint","IMPRINT",FACE,{"disambiguationData":[TD([[makeQuery(id+"F2.imprint","IMPRINT",EDGE,{"derivedFrom":sQuery(id+"F2.wireOp",EDGE,"E42.23")}),-1.0]])]});
            var Q16;
            Q16=makeQuery(id+"F2.imprint","IMPRINT",FACE,{"disambiguationData":[TD([[makeQuery(id+"F2.imprint","IMPRINT",EDGE,{"derivedFrom":sQuery(id+"F2.wireOp",EDGE,"E42.30")}),1.0]])]});
            var Q17;
            Q17=makeQuery(id+"F2.imprint","IMPRINT",FACE,{"disambiguationData":[TD([[makeQuery(id+"F2.imprint","IMPRINT",EDGE,{"derivedFrom":sQuery(id+"F2.wireOp",EDGE,"E42.28")}),1.0]])]});
            var Q18;
            Q18=makeQuery(id+"F2.imprint","IMPRINT",FACE,{"disambiguationData":[TD([[makeQuery(id+"F2.imprint","IMPRINT",EDGE,{"derivedFrom":sQuery(id+"F2.wireOp",EDGE,"E42.28")}),-1.0]])]});
            var Q19;
            {var subQ0=sQuery(id+"F2.wireOp",EDGE,"E42.50");Q19=makeQuery(id+"F2.imprint","IMPRINT",FACE,{"disambiguationData":[TD([[makeQuery(id+"F2.imprint","IMPRINT",EDGE,{"derivedFrom":subQ0}),1.0]])]});}
            var Q20;
            {var subQ0=sQuery(id+"F2.wireOp",EDGE,"E42.49");Q20=makeQuery(id+"F2.imprint","IMPRINT",FACE,{"disambiguationData":[TD([[makeQuery(id+"F2.imprint","IMPRINT",EDGE,{"derivedFrom":subQ0}),1.0]])]});}
            extrude(context, id + "F3", {"entities" : qUnion([Q0, Q1, Q2, Q3, Q4, Q5, Q6, Q7, Q8, Q9, Q10, Q11, Q12, Q13, Q14, Q15, Q16, Q17, Q18, Q19, Q20]), "operationType" : NewBodyOperationType.ADD, "depth" : 10 * mm});
        }
        {
            var Q0;
            Q0=makeQuery(id+"F3.opExtrude","CAP_FACE",FACE,{"disambiguationData":[OSD([sQuery(id+"F2.wireOp",EDGE,"E42.0"),sQuery(id+"F2.wireOp",EDGE,"E42.1"),sQuery(id+"F2.wireOp",EDGE,"E42.2"),sQuery(id+"F2.wireOp",EDGE,"E42.3"),sQuery(id+"F2.wireOp",EDGE,"E42.6"),sQuery(id+"F2.wireOp",EDGE,"E42.8"),sQuery(id+"F2.wireOp",EDGE,"E42.10"),sQuery(id+"F2.wireOp",EDGE,"E42.12"),sQuery(id+"F2.wireOp",EDGE,"E42.46"),sQuery(id+"F2.wireOp",EDGE,"E42.47")])],"isStart":false});
            extrude(context, id + "F4", {"entities" : qUnion([Q0]), "operationType" : NewBodyOperationType.ADD, "depth" : 25 * mm});
        }
    });
